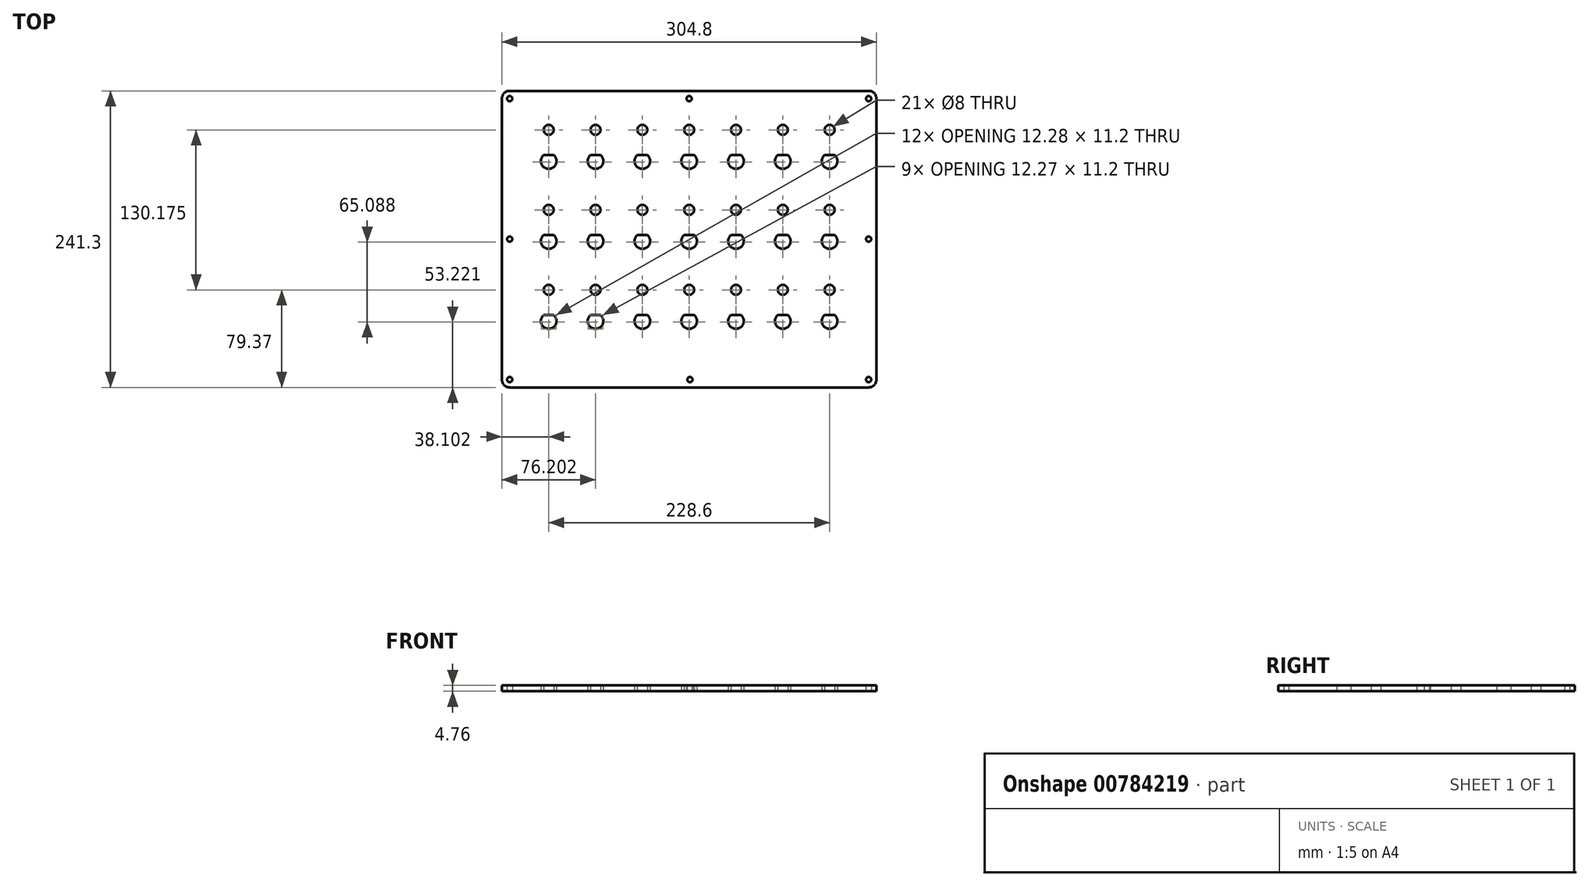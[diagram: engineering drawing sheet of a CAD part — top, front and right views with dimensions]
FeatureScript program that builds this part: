
annotation { "Feature Type Name" : "Feature", "Feature Type Description" : "" }
export const myFeature = defineFeature(function(context is Context, id is Id, definition is map)
    precondition{}
    {
        {
            var Q0;
            Q0=qCreatedBy(makeId("Top.planeOp"),FACE);
            var sketch = newSketch(context, id + "F0", { "sketchPlane" : qUnion([Q0])});
            skPoint(sketch, "E0", {"position": v(-117.79, 114.33) * mm});
            skLineSegment(sketch, "E1.bottom", {"start": v(-149.54, 146.08) * mm, "end": v(142.56, 146.08) * mm});
            skLineSegment(sketch, "E1.top", {"start": v(-149.54, -95.22) * mm, "end": v(142.56, -95.22) * mm});
            skLineSegment(sketch, "E1.left", {"start": v(-155.89, 139.73) * mm, "end": v(-155.89, -88.87) * mm});
            skLineSegment(sketch, "E1.right", {"start": v(148.91, 139.73) * mm, "end": v(148.91, -88.87) * mm});
            skPoint(sketch, "E2", {"position": v(-149.54, 139.73) * mm});
            skPoint(sketch, "E3", {"position": v(142.56, 139.73) * mm});
            skPoint(sketch, "E4", {"position": v(142.56, -88.87) * mm});
            skPoint(sketch, "E5", {"position": v(-149.54, -88.87) * mm});
            skPoint(sketch, "E6", {"position": v(-3.49, 139.73) * mm});
            skPoint(sketch, "E7", {"position": v(-2.85, -88.87) * mm});
            skCircle(sketch, "E8", {"center": v(-117.79, 88.93) * mm, "radius": 6.35 * mm});
            skLineSegment(sketch, "E9", {"start": v(-121.89, 93.78) * mm, "end": v(-113.7, 93.78) * mm});
            skCircle(sketch, "E10.0.1.0", {"center": v(-117.79, 23.84) * mm, "radius": 6.35 * mm});
            skPoint(sketch, "E10.0.1.1", {"position": v(-117.79, 49.24) * mm});
            skLineSegment(sketch, "E10.0.1.2", {"start": v(-121.89, 28.69) * mm, "end": v(-113.7, 28.69) * mm});
            skCircle(sketch, "E10.0.2.0", {"center": v(-117.79, -41.25) * mm, "radius": 6.35 * mm});
            skPoint(sketch, "E10.0.2.1", {"position": v(-117.79, -15.85) * mm});
            skLineSegment(sketch, "E10.0.2.2", {"start": v(-121.89, -36.4) * mm, "end": v(-113.7, -36.4) * mm});
            skCircle(sketch, "E10.1.0.0", {"center": v(-79.69, 88.93) * mm, "radius": 6.35 * mm});
            skPoint(sketch, "E10.1.0.1", {"position": v(-79.69, 114.33) * mm});
            skLineSegment(sketch, "E10.1.0.2", {"start": v(-83.79, 93.78) * mm, "end": v(-75.6, 93.78) * mm});
            skCircle(sketch, "E10.1.1.0", {"center": v(-79.69, 23.84) * mm, "radius": 6.35 * mm});
            skPoint(sketch, "E10.1.1.1", {"position": v(-79.69, 49.24) * mm});
            skLineSegment(sketch, "E10.1.1.2", {"start": v(-83.79, 28.69) * mm, "end": v(-75.6, 28.69) * mm});
            skCircle(sketch, "E10.1.2.0", {"center": v(-79.69, -41.25) * mm, "radius": 6.35 * mm});
            skPoint(sketch, "E10.1.2.1", {"position": v(-79.69, -15.85) * mm});
            skLineSegment(sketch, "E10.1.2.2", {"start": v(-83.79, -36.4) * mm, "end": v(-75.6, -36.4) * mm});
            skCircle(sketch, "E10.2.0.0", {"center": v(-41.59, 88.93) * mm, "radius": 6.35 * mm});
            skPoint(sketch, "E10.2.0.1", {"position": v(-41.59, 114.33) * mm});
            skLineSegment(sketch, "E10.2.0.2", {"start": v(-45.69, 93.78) * mm, "end": v(-37.5, 93.78) * mm});
            skCircle(sketch, "E10.2.1.0", {"center": v(-41.59, 23.84) * mm, "radius": 6.35 * mm});
            skPoint(sketch, "E10.2.1.1", {"position": v(-41.59, 49.24) * mm});
            skLineSegment(sketch, "E10.2.1.2", {"start": v(-45.69, 28.69) * mm, "end": v(-37.5, 28.69) * mm});
            skCircle(sketch, "E10.2.2.0", {"center": v(-41.59, -41.25) * mm, "radius": 6.35 * mm});
            skPoint(sketch, "E10.2.2.1", {"position": v(-41.59, -15.85) * mm});
            skLineSegment(sketch, "E10.2.2.2", {"start": v(-45.69, -36.4) * mm, "end": v(-37.5, -36.4) * mm});
            skCircle(sketch, "E10.3.0.0", {"center": v(-3.49, 88.93) * mm, "radius": 6.35 * mm});
            skPoint(sketch, "E10.3.0.1", {"position": v(-3.49, 114.33) * mm});
            skLineSegment(sketch, "E10.3.0.2", {"start": v(-7.59, 93.78) * mm, "end": v(0.6, 93.78) * mm});
            skCircle(sketch, "E10.3.1.0", {"center": v(-3.49, 23.84) * mm, "radius": 6.35 * mm});
            skPoint(sketch, "E10.3.1.1", {"position": v(-3.49, 49.24) * mm});
            skLineSegment(sketch, "E10.3.1.2", {"start": v(-7.59, 28.69) * mm, "end": v(0.6, 28.69) * mm});
            skCircle(sketch, "E10.3.2.0", {"center": v(-3.49, -41.25) * mm, "radius": 6.35 * mm});
            skPoint(sketch, "E10.3.2.1", {"position": v(-3.49, -15.85) * mm});
            skLineSegment(sketch, "E10.3.2.2", {"start": v(-7.59, -36.4) * mm, "end": v(0.6, -36.4) * mm});
            skCircle(sketch, "E10.4.0.0", {"center": v(34.61, 88.93) * mm, "radius": 6.35 * mm});
            skPoint(sketch, "E10.4.0.1", {"position": v(34.61, 114.33) * mm});
            skLineSegment(sketch, "E10.4.0.2", {"start": v(30.51, 93.78) * mm, "end": v(38.7, 93.78) * mm});
            skCircle(sketch, "E10.4.1.0", {"center": v(34.61, 23.84) * mm, "radius": 6.35 * mm});
            skPoint(sketch, "E10.4.1.1", {"position": v(34.61, 49.24) * mm});
            skLineSegment(sketch, "E10.4.1.2", {"start": v(30.51, 28.69) * mm, "end": v(38.7, 28.69) * mm});
            skCircle(sketch, "E10.4.2.0", {"center": v(34.61, -41.25) * mm, "radius": 6.35 * mm});
            skPoint(sketch, "E10.4.2.1", {"position": v(34.61, -15.85) * mm});
            skLineSegment(sketch, "E10.4.2.2", {"start": v(30.51, -36.4) * mm, "end": v(38.7, -36.4) * mm});
            skCircle(sketch, "E10.5.0.0", {"center": v(72.71, 88.93) * mm, "radius": 6.35 * mm});
            skPoint(sketch, "E10.5.0.1", {"position": v(72.71, 114.33) * mm});
            skLineSegment(sketch, "E10.5.0.2", {"start": v(68.61, 93.78) * mm, "end": v(76.8, 93.78) * mm});
            skCircle(sketch, "E10.5.1.0", {"center": v(72.71, 23.84) * mm, "radius": 6.35 * mm});
            skPoint(sketch, "E10.5.1.1", {"position": v(72.71, 49.24) * mm});
            skLineSegment(sketch, "E10.5.1.2", {"start": v(68.61, 28.69) * mm, "end": v(76.8, 28.69) * mm});
            skCircle(sketch, "E10.5.2.0", {"center": v(72.71, -41.25) * mm, "radius": 6.35 * mm});
            skPoint(sketch, "E10.5.2.1", {"position": v(72.71, -15.85) * mm});
            skLineSegment(sketch, "E10.5.2.2", {"start": v(68.61, -36.4) * mm, "end": v(76.8, -36.4) * mm});
            skCircle(sketch, "E10.6.0.0", {"center": v(110.81, 88.93) * mm, "radius": 6.35 * mm});
            skPoint(sketch, "E10.6.0.1", {"position": v(110.81, 114.33) * mm});
            skLineSegment(sketch, "E10.6.0.2", {"start": v(106.71, 93.78) * mm, "end": v(114.9, 93.78) * mm});
            skCircle(sketch, "E10.6.1.0", {"center": v(110.81, 23.84) * mm, "radius": 6.35 * mm});
            skPoint(sketch, "E10.6.1.1", {"position": v(110.81, 49.24) * mm});
            skLineSegment(sketch, "E10.6.1.2", {"start": v(106.71, 28.69) * mm, "end": v(114.9, 28.69) * mm});
            skCircle(sketch, "E10.6.2.0", {"center": v(110.81, -41.25) * mm, "radius": 6.35 * mm});
            skPoint(sketch, "E10.6.2.1", {"position": v(110.81, -15.85) * mm});
            skLineSegment(sketch, "E10.6.2.2", {"start": v(106.71, -36.4) * mm, "end": v(114.9, -36.4) * mm});
            skLineSegment(sketch, "E10.direction1", {"start": v(-117.79, 88.93) * mm, "end": v(-79.69, 88.93) * mm, "construction": true});
            skLineSegment(sketch, "E10.direction2", {"start": v(-117.79, 88.93) * mm, "end": v(-117.79, 23.84) * mm, "construction": true});
            skPoint(sketch, "E11", {"position": v(-149.54, 25.43) * mm});
            skPoint(sketch, "E12", {"position": v(142.56, 25.43) * mm});
            skPoint(sketch, "E13.visualSharp", {"position": v(-155.89, 146.08) * mm});
            skArc(sketch, "E13.filletArc", {"start": v(-149.54, 146.08) * mm, "mid": v(-154.03, 144.22) * mm, "end": v(-155.89, 139.73) * mm});
            skPoint(sketch, "E14.visualSharp", {"position": v(-155.89, -95.22) * mm});
            skArc(sketch, "E14.filletArc", {"start": v(-155.89, -88.87) * mm, "mid": v(-154.03, -93.36) * mm, "end": v(-149.54, -95.22) * mm});
            skPoint(sketch, "E15.visualSharp", {"position": v(148.91, -95.22) * mm});
            skArc(sketch, "E15.filletArc", {"start": v(142.56, -95.22) * mm, "mid": v(147.05, -93.36) * mm, "end": v(148.91, -88.87) * mm});
            skPoint(sketch, "E16.visualSharp", {"position": v(148.91, 146.08) * mm});
            skArc(sketch, "E16.filletArc", {"start": v(148.91, 139.73) * mm, "mid": v(147.05, 144.22) * mm, "end": v(142.56, 146.08) * mm});
            skSolve(sketch);
        }
        {
            var Q0;
            Q0=makeQuery(id+"F0.imprint","IMPRINT",FACE,{"disambiguationData":[TD([[makeQuery(id+"F0.imprint","IMPRINT",EDGE,{"derivedFrom":sQuery(id+"F0.wireOp",EDGE,"E1.bottom")}),-1.0]])]});
            var Q1;
            {var subQ0=sQuery(id+"F0.wireOp",EDGE,"E10.2.0.2");Q1=makeQuery(id+"F0.imprint","IMPRINT",FACE,{"disambiguationData":[TD([[makeQuery(id+"F0.imprint","IMPRINT",EDGE,{"derivedFrom":subQ0}),1.0]])]});}
            var Q2;
            {var subQ0=sQuery(id+"F0.wireOp",EDGE,"E9");Q2=makeQuery(id+"F0.imprint","IMPRINT",FACE,{"disambiguationData":[TD([[makeQuery(id+"F0.imprint","IMPRINT",EDGE,{"derivedFrom":subQ0}),1.0]])]});}
            var Q3;
            {var subQ0=sQuery(id+"F0.wireOp",EDGE,"E10.1.0.2");Q3=makeQuery(id+"F0.imprint","IMPRINT",FACE,{"disambiguationData":[TD([[makeQuery(id+"F0.imprint","IMPRINT",EDGE,{"derivedFrom":subQ0}),1.0]])]});}
            var Q4;
            {var subQ0=sQuery(id+"F0.wireOp",EDGE,"E10.5.0.2");Q4=makeQuery(id+"F0.imprint","IMPRINT",FACE,{"disambiguationData":[TD([[makeQuery(id+"F0.imprint","IMPRINT",EDGE,{"derivedFrom":subQ0}),1.0]])]});}
            var Q5;
            {var subQ0=sQuery(id+"F0.wireOp",EDGE,"E10.6.0.2");Q5=makeQuery(id+"F0.imprint","IMPRINT",FACE,{"disambiguationData":[TD([[makeQuery(id+"F0.imprint","IMPRINT",EDGE,{"derivedFrom":subQ0}),1.0]])]});}
            var Q6;
            {var subQ0=sQuery(id+"F0.wireOp",EDGE,"E10.4.0.2");Q6=makeQuery(id+"F0.imprint","IMPRINT",FACE,{"disambiguationData":[TD([[makeQuery(id+"F0.imprint","IMPRINT",EDGE,{"derivedFrom":subQ0}),1.0]])]});}
            var Q7;
            {var subQ0=sQuery(id+"F0.wireOp",EDGE,"E10.3.0.2");Q7=makeQuery(id+"F0.imprint","IMPRINT",FACE,{"disambiguationData":[TD([[makeQuery(id+"F0.imprint","IMPRINT",EDGE,{"derivedFrom":subQ0}),1.0]])]});}
            var Q8;
            {var subQ0=sQuery(id+"F0.wireOp",EDGE,"E10.6.1.2");Q8=makeQuery(id+"F0.imprint","IMPRINT",FACE,{"disambiguationData":[TD([[makeQuery(id+"F0.imprint","IMPRINT",EDGE,{"derivedFrom":subQ0}),1.0]])]});}
            var Q9;
            {var subQ0=sQuery(id+"F0.wireOp",EDGE,"E10.5.1.2");Q9=makeQuery(id+"F0.imprint","IMPRINT",FACE,{"disambiguationData":[TD([[makeQuery(id+"F0.imprint","IMPRINT",EDGE,{"derivedFrom":subQ0}),1.0]])]});}
            var Q10;
            {var subQ0=sQuery(id+"F0.wireOp",EDGE,"E10.0.1.2");Q10=makeQuery(id+"F0.imprint","IMPRINT",FACE,{"disambiguationData":[TD([[makeQuery(id+"F0.imprint","IMPRINT",EDGE,{"derivedFrom":subQ0}),1.0]])]});}
            var Q11;
            {var subQ0=sQuery(id+"F0.wireOp",EDGE,"E10.1.1.2");Q11=makeQuery(id+"F0.imprint","IMPRINT",FACE,{"disambiguationData":[TD([[makeQuery(id+"F0.imprint","IMPRINT",EDGE,{"derivedFrom":subQ0}),1.0]])]});}
            var Q12;
            {var subQ0=sQuery(id+"F0.wireOp",EDGE,"E10.4.1.2");Q12=makeQuery(id+"F0.imprint","IMPRINT",FACE,{"disambiguationData":[TD([[makeQuery(id+"F0.imprint","IMPRINT",EDGE,{"derivedFrom":subQ0}),1.0]])]});}
            var Q13;
            {var subQ0=sQuery(id+"F0.wireOp",EDGE,"E10.2.1.2");Q13=makeQuery(id+"F0.imprint","IMPRINT",FACE,{"disambiguationData":[TD([[makeQuery(id+"F0.imprint","IMPRINT",EDGE,{"derivedFrom":subQ0}),1.0]])]});}
            var Q14;
            {var subQ0=sQuery(id+"F0.wireOp",EDGE,"E10.3.1.2");Q14=makeQuery(id+"F0.imprint","IMPRINT",FACE,{"disambiguationData":[TD([[makeQuery(id+"F0.imprint","IMPRINT",EDGE,{"derivedFrom":subQ0}),1.0]])]});}
            var Q15;
            {var subQ0=sQuery(id+"F0.wireOp",EDGE,"E10.1.2.2");Q15=makeQuery(id+"F0.imprint","IMPRINT",FACE,{"disambiguationData":[TD([[makeQuery(id+"F0.imprint","IMPRINT",EDGE,{"derivedFrom":subQ0}),1.0]])]});}
            var Q16;
            {var subQ0=sQuery(id+"F0.wireOp",EDGE,"E10.0.2.2");Q16=makeQuery(id+"F0.imprint","IMPRINT",FACE,{"disambiguationData":[TD([[makeQuery(id+"F0.imprint","IMPRINT",EDGE,{"derivedFrom":subQ0}),1.0]])]});}
            var Q17;
            {var subQ0=sQuery(id+"F0.wireOp",EDGE,"E10.6.2.2");Q17=makeQuery(id+"F0.imprint","IMPRINT",FACE,{"disambiguationData":[TD([[makeQuery(id+"F0.imprint","IMPRINT",EDGE,{"derivedFrom":subQ0}),1.0]])]});}
            var Q18;
            {var subQ0=sQuery(id+"F0.wireOp",EDGE,"E10.2.2.2");Q18=makeQuery(id+"F0.imprint","IMPRINT",FACE,{"disambiguationData":[TD([[makeQuery(id+"F0.imprint","IMPRINT",EDGE,{"derivedFrom":subQ0}),1.0]])]});}
            var Q19;
            {var subQ0=sQuery(id+"F0.wireOp",EDGE,"E10.4.2.2");Q19=makeQuery(id+"F0.imprint","IMPRINT",FACE,{"disambiguationData":[TD([[makeQuery(id+"F0.imprint","IMPRINT",EDGE,{"derivedFrom":subQ0}),1.0]])]});}
            var Q20;
            {var subQ0=sQuery(id+"F0.wireOp",EDGE,"E10.5.2.2");Q20=makeQuery(id+"F0.imprint","IMPRINT",FACE,{"disambiguationData":[TD([[makeQuery(id+"F0.imprint","IMPRINT",EDGE,{"derivedFrom":subQ0}),1.0]])]});}
            var Q21;
            {var subQ0=sQuery(id+"F0.wireOp",EDGE,"E10.3.2.2");Q21=makeQuery(id+"F0.imprint","IMPRINT",FACE,{"disambiguationData":[TD([[makeQuery(id+"F0.imprint","IMPRINT",EDGE,{"derivedFrom":subQ0}),1.0]])]});}
            extrude(context, id + "F1", {"entities" : qUnion([Q0, Q1, Q2, Q3, Q4, Q5, Q6, Q7, Q8, Q9, Q10, Q11, Q12, Q13, Q14, Q15, Q16, Q17, Q18, Q19, Q20, Q21]), "depth" : 4.76 * mm, "offsetDistance" : 25.4 * mm});
        }
        {
            var Q0;
            Q0=sQuery(id+"F0.wireOp",VERTEX,"E10.4.0.1");
            var Q1;
            Q1=sQuery(id+"F0.wireOp",VERTEX,"E10.6.0.1");
            var Q2;
            Q2=sQuery(id+"F0.wireOp",VERTEX,"E10.2.0.1");
            var Q3;
            Q3=sQuery(id+"F0.wireOp",VERTEX,"E0");
            var Q4;
            Q4=sQuery(id+"F0.wireOp",VERTEX,"E10.3.0.1");
            var Q5;
            Q5=sQuery(id+"F0.wireOp",VERTEX,"E10.5.0.1");
            var Q6;
            Q6=sQuery(id+"F0.wireOp",VERTEX,"E10.1.0.1");
            var Q7;
            Q7=sQuery(id+"F0.wireOp",VERTEX,"E10.2.1.1");
            var Q8;
            Q8=sQuery(id+"F0.wireOp",VERTEX,"E10.4.1.1");
            var Q9;
            Q9=sQuery(id+"F0.wireOp",VERTEX,"E10.6.1.1");
            var Q10;
            Q10=sQuery(id+"F0.wireOp",VERTEX,"E10.1.1.1");
            var Q11;
            Q11=sQuery(id+"F0.wireOp",VERTEX,"E10.3.1.1");
            var Q12;
            Q12=sQuery(id+"F0.wireOp",VERTEX,"E10.5.1.1");
            var Q13;
            Q13=sQuery(id+"F0.wireOp",VERTEX,"E10.0.1.1");
            var Q14;
            Q14=sQuery(id+"F0.wireOp",VERTEX,"E10.2.2.1");
            var Q15;
            Q15=sQuery(id+"F0.wireOp",VERTEX,"E10.5.2.1");
            var Q16;
            Q16=sQuery(id+"F0.wireOp",VERTEX,"E10.1.2.1");
            var Q17;
            Q17=sQuery(id+"F0.wireOp",VERTEX,"E10.3.2.1");
            var Q18;
            Q18=sQuery(id+"F0.wireOp",VERTEX,"E10.0.2.1");
            var Q19;
            Q19=sQuery(id+"F0.wireOp",VERTEX,"E10.4.2.1");
            var Q20;
            Q20=sQuery(id+"F0.wireOp",VERTEX,"E10.6.2.1");
            var Q21;
            Q21=makeQuery(id+"F1.opExtrude","SWEPT_BODY",BODY,{"disambiguationData":[OSD([sQuery(id+"F0.wireOp",EDGE,"E1.bottom"),sQuery(id+"F0.wireOp",EDGE,"E1.top"),sQuery(id+"F0.wireOp",EDGE,"E1.left"),sQuery(id+"F0.wireOp",EDGE,"E1.right"),sQuery(id+"F0.wireOp",EDGE,"E8"),sQuery(id+"F0.wireOp",EDGE,"E9"),sQuery(id+"F0.wireOp",EDGE,"E10.0.1.0"),sQuery(id+"F0.wireOp",EDGE,"E10.0.1.2"),sQuery(id+"F0.wireOp",EDGE,"E10.0.2.0"),sQuery(id+"F0.wireOp",EDGE,"E10.0.2.2"),sQuery(id+"F0.wireOp",EDGE,"E10.1.0.0"),sQuery(id+"F0.wireOp",EDGE,"E10.1.0.2"),sQuery(id+"F0.wireOp",EDGE,"E10.1.1.0"),sQuery(id+"F0.wireOp",EDGE,"E10.1.1.2"),sQuery(id+"F0.wireOp",EDGE,"E10.1.2.0"),sQuery(id+"F0.wireOp",EDGE,"E10.1.2.2"),sQuery(id+"F0.wireOp",EDGE,"E10.2.0.0"),sQuery(id+"F0.wireOp",EDGE,"E10.2.0.2"),sQuery(id+"F0.wireOp",EDGE,"E10.2.1.0"),sQuery(id+"F0.wireOp",EDGE,"E10.2.1.2"),sQuery(id+"F0.wireOp",EDGE,"E10.2.2.0"),sQuery(id+"F0.wireOp",EDGE,"E10.2.2.2"),sQuery(id+"F0.wireOp",EDGE,"E10.3.0.0"),sQuery(id+"F0.wireOp",EDGE,"E10.3.0.2"),sQuery(id+"F0.wireOp",EDGE,"E10.3.1.0"),sQuery(id+"F0.wireOp",EDGE,"E10.3.1.2"),sQuery(id+"F0.wireOp",EDGE,"E10.3.2.0"),sQuery(id+"F0.wireOp",EDGE,"E10.3.2.2"),sQuery(id+"F0.wireOp",EDGE,"E10.4.0.0"),sQuery(id+"F0.wireOp",EDGE,"E10.4.0.2"),sQuery(id+"F0.wireOp",EDGE,"E10.4.1.0"),sQuery(id+"F0.wireOp",EDGE,"E10.4.1.2"),sQuery(id+"F0.wireOp",EDGE,"E10.4.2.0"),sQuery(id+"F0.wireOp",EDGE,"E10.4.2.2"),sQuery(id+"F0.wireOp",EDGE,"E10.5.0.0"),sQuery(id+"F0.wireOp",EDGE,"E10.5.0.2"),sQuery(id+"F0.wireOp",EDGE,"E10.5.1.0"),sQuery(id+"F0.wireOp",EDGE,"E10.5.1.2"),sQuery(id+"F0.wireOp",EDGE,"E10.5.2.0"),sQuery(id+"F0.wireOp",EDGE,"E10.5.2.2"),sQuery(id+"F0.wireOp",EDGE,"E10.6.0.0"),sQuery(id+"F0.wireOp",EDGE,"E10.6.0.2"),sQuery(id+"F0.wireOp",EDGE,"E10.6.1.0"),sQuery(id+"F0.wireOp",EDGE,"E10.6.1.2"),sQuery(id+"F0.wireOp",EDGE,"E10.6.2.0"),sQuery(id+"F0.wireOp",EDGE,"E10.6.2.2"),sQuery(id+"F0.wireOp",EDGE,"E13.filletArc"),sQuery(id+"F0.wireOp",EDGE,"E14.filletArc"),sQuery(id+"F0.wireOp",EDGE,"E15.filletArc"),sQuery(id+"F0.wireOp",EDGE,"E16.filletArc")])]});
            hole(context, id + "F2", {"style" : HoleStyle.SIMPLE, "endStyle" : HoleEndStyle.THROUGH, "oppositeDirection" : true, "holeDiameter" : 8 * mm, "majorDiameter" : 6.35 * mm, "isTappedThrough" : true, "tappedDepth" : 12.7 * mm, "tapClearance" : 3, "locations" : qUnion([Q0, Q1, Q2, Q3, Q4, Q5, Q6, Q7, Q8, Q9, Q10, Q11, Q12, Q13, Q14, Q15, Q16, Q17, Q18, Q19, Q20]), "scope" : qUnion([Q21])});
        }
        {
            var Q0;
            Q0=sQuery(id+"F0.wireOp",VERTEX,"E5");
            var Q1;
            Q1=sQuery(id+"F0.wireOp",VERTEX,"E11");
            var Q2;
            Q2=sQuery(id+"F0.wireOp",VERTEX,"E2");
            var Q3;
            Q3=sQuery(id+"F0.wireOp",VERTEX,"E7");
            var Q4;
            Q4=sQuery(id+"F0.wireOp",VERTEX,"E4");
            var Q5;
            Q5=sQuery(id+"F0.wireOp",VERTEX,"E12");
            var Q6;
            Q6=sQuery(id+"F0.wireOp",VERTEX,"E3");
            var Q7;
            Q7=sQuery(id+"F0.wireOp",VERTEX,"E6");
            var Q8;
            Q8=makeQuery(id+"F1.opExtrude","SWEPT_BODY",BODY,{"disambiguationData":[OSD([sQuery(id+"F0.wireOp",EDGE,"eEAdmfjY-mWAV-G8b8-mztT-bruEK4ECARcJ"),sQuery(id+"F0.wireOp",EDGE,"60gL4Slp-9RgS-x02q-Mukb-vAcMxLebmuDx"),sQuery(id+"F0.wireOp",EDGE,"73908852-a9be-43a3-a854-593b25c4470a.0.1.0"),sQuery(id+"F0.wireOp",EDGE,"73908852-a9be-43a3-a854-593b25c4470a.0.1.3"),sQuery(id+"F0.wireOp",EDGE,"73908852-a9be-43a3-a854-593b25c4470a.0.2.0"),sQuery(id+"F0.wireOp",EDGE,"73908852-a9be-43a3-a854-593b25c4470a.0.2.3"),sQuery(id+"F0.wireOp",EDGE,"73908852-a9be-43a3-a854-593b25c4470a.1.0.0"),sQuery(id+"F0.wireOp",EDGE,"73908852-a9be-43a3-a854-593b25c4470a.1.0.3"),sQuery(id+"F0.wireOp",EDGE,"73908852-a9be-43a3-a854-593b25c4470a.1.1.0"),sQuery(id+"F0.wireOp",EDGE,"73908852-a9be-43a3-a854-593b25c4470a.1.1.3"),sQuery(id+"F0.wireOp",EDGE,"73908852-a9be-43a3-a854-593b25c4470a.1.2.0"),sQuery(id+"F0.wireOp",EDGE,"73908852-a9be-43a3-a854-593b25c4470a.1.2.3"),sQuery(id+"F0.wireOp",EDGE,"73908852-a9be-43a3-a854-593b25c4470a.2.0.0"),sQuery(id+"F0.wireOp",EDGE,"73908852-a9be-43a3-a854-593b25c4470a.2.0.3"),sQuery(id+"F0.wireOp",EDGE,"73908852-a9be-43a3-a854-593b25c4470a.2.1.0"),sQuery(id+"F0.wireOp",EDGE,"73908852-a9be-43a3-a854-593b25c4470a.2.1.3"),sQuery(id+"F0.wireOp",EDGE,"73908852-a9be-43a3-a854-593b25c4470a.2.2.0"),sQuery(id+"F0.wireOp",EDGE,"73908852-a9be-43a3-a854-593b25c4470a.2.2.3"),sQuery(id+"F0.wireOp",EDGE,"73908852-a9be-43a3-a854-593b25c4470a.3.0.0"),sQuery(id+"F0.wireOp",EDGE,"73908852-a9be-43a3-a854-593b25c4470a.3.0.3"),sQuery(id+"F0.wireOp",EDGE,"73908852-a9be-43a3-a854-593b25c4470a.3.1.0"),sQuery(id+"F0.wireOp",EDGE,"73908852-a9be-43a3-a854-593b25c4470a.3.1.3"),sQuery(id+"F0.wireOp",EDGE,"73908852-a9be-43a3-a854-593b25c4470a.3.2.0"),sQuery(id+"F0.wireOp",EDGE,"73908852-a9be-43a3-a854-593b25c4470a.3.2.3"),sQuery(id+"F0.wireOp",EDGE,"73908852-a9be-43a3-a854-593b25c4470a.4.0.0"),sQuery(id+"F0.wireOp",EDGE,"73908852-a9be-43a3-a854-593b25c4470a.4.0.3"),sQuery(id+"F0.wireOp",EDGE,"73908852-a9be-43a3-a854-593b25c4470a.4.1.0"),sQuery(id+"F0.wireOp",EDGE,"73908852-a9be-43a3-a854-593b25c4470a.4.1.3"),sQuery(id+"F0.wireOp",EDGE,"73908852-a9be-43a3-a854-593b25c4470a.4.2.0"),sQuery(id+"F0.wireOp",EDGE,"73908852-a9be-43a3-a854-593b25c4470a.4.2.3"),sQuery(id+"F0.wireOp",EDGE,"73908852-a9be-43a3-a854-593b25c4470a.5.0.0"),sQuery(id+"F0.wireOp",EDGE,"73908852-a9be-43a3-a854-593b25c4470a.5.0.3"),sQuery(id+"F0.wireOp",EDGE,"73908852-a9be-43a3-a854-593b25c4470a.5.1.0"),sQuery(id+"F0.wireOp",EDGE,"73908852-a9be-43a3-a854-593b25c4470a.5.1.3"),sQuery(id+"F0.wireOp",EDGE,"73908852-a9be-43a3-a854-593b25c4470a.5.2.0"),sQuery(id+"F0.wireOp",EDGE,"73908852-a9be-43a3-a854-593b25c4470a.5.2.3"),sQuery(id+"F0.wireOp",EDGE,"73908852-a9be-43a3-a854-593b25c4470a.6.0.0"),sQuery(id+"F0.wireOp",EDGE,"73908852-a9be-43a3-a854-593b25c4470a.6.0.3"),sQuery(id+"F0.wireOp",EDGE,"73908852-a9be-43a3-a854-593b25c4470a.6.1.0"),sQuery(id+"F0.wireOp",EDGE,"73908852-a9be-43a3-a854-593b25c4470a.6.1.3"),sQuery(id+"F0.wireOp",EDGE,"73908852-a9be-43a3-a854-593b25c4470a.6.2.0"),sQuery(id+"F0.wireOp",EDGE,"73908852-a9be-43a3-a854-593b25c4470a.6.2.3"),sQuery(id+"F0.wireOp",EDGE,"E1.bottom"),sQuery(id+"F0.wireOp",EDGE,"E1.top"),sQuery(id+"F0.wireOp",EDGE,"E1.left"),sQuery(id+"F0.wireOp",EDGE,"E1.right")])]});
            hole(context, id + "F3", {"style" : HoleStyle.SIMPLE, "endStyle" : HoleEndStyle.THROUGH, "oppositeDirection" : true, "holeDiameter" : 4.17 * mm, "majorDiameter" : 6.35 * mm, "isTappedThrough" : true, "tappedDepth" : 12.7 * mm, "tapClearance" : 3, "locations" : qUnion([Q0, Q1, Q2, Q3, Q4, Q5, Q6, Q7]), "scope" : qUnion([Q8])});
        }
    });
